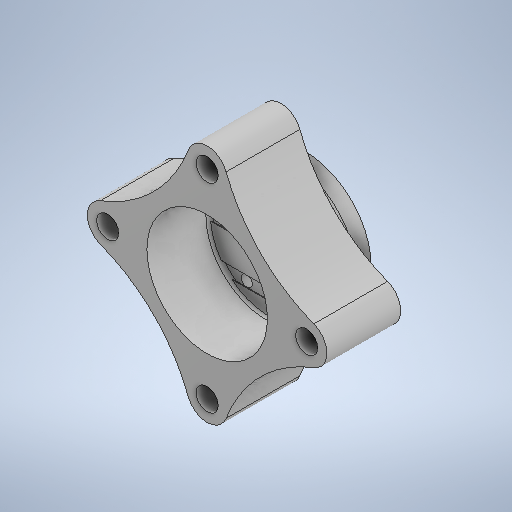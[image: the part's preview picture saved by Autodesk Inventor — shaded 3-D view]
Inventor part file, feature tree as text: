
AUTODESK INVENTOR PART (.ipt)
format: ipt  version: 2025.2 (Build 292293000, 293)  size: 745,984 bytes
history: native  units: in
note: dims shown in document units (in); Inventor stores cm internally (conversion verified against a paired STEP export)
features: sketch x16, extrude x13, projected_geometry x4, fillet x2, plane x1
ambient origin geometry x8: Origin, YZ Plane, XZ Plane, XY Plane, X Axis, Y Axis, Z Axis, Center Point
bodies: Solid1 (feature_tree), Body3 (feature_tree)
feature tree (36):
  extrude  "Extrusion1"  Depth=0.3937in TaperAngle=0.0deg
  extrude  "Extrusion2"  [1 undecoded]
  extrude  "Extrusion3"  Depth=0.315in TaperAngle=0.0deg
  plane  "Work Plane1"
  extrude  "Extrusion4"  Depth=0.2362in
  sketch  "Sketch5"  dims[d21=0.4724in d22=0.0in d23=0.0591in d24=0.0in]
  extrude  "Extrusion5"  TaperAngle=0.0deg  [1 undecoded]
  extrude  "Extrusion6"  Depth=0.3937in TaperAngle=0.0deg
  extrude  "Extrusion7"  Depth=0.0591in TaperAngle=0.0deg
  extrude  "Extrusion8"  Depth=0.1654in
  extrude  "Extrusion9"  TaperAngle=0.0deg  [1 undecoded]
  extrude  "Extrusion10"  Depth=0.1181in
  fillet  "Fillet1"  Radius=0.1181in
  extrude  "Extrusion11"  Depth=0.1181in
  extrude  "Extrusion12"  TaperAngle=0.0deg  [1 undecoded]
  fillet  "Fillet2"  Radius=0.0984in
  extrude  "Extrusion13"  TaperAngle=0.0deg  [1 undecoded]
  sketch  "Sketch1"  dims[d0=0.3937in d1=0.0in d2=0.3937in d3=0.0in]
  sketch  "Sketch2"  dims[d7=2.5591in d8=0.315in d9=0.0in]
  projected_geometry  "Projected Loop1"
  sketch  "Sketch3"  dims[d12=1.5748in d14=360.0deg d16=0.0in d17=0.0in]
  sketch  "Sketch4"  dims[d18=0.1181in d19=0.3937in d20=0.0in]
  sketch  "Sketch6"  dims[d25=0.1654in d26=0.1654in]
  sketch  "Sketch Circular Pattern1"  dims[d4=0.3937in d5=0.0in d6=-0.1181in]
  sketch  "Sketch7"  dims[d27=0.1654in d28=0.0in d29=0.0in]
  sketch  "Sketch8"  dims[d30=0.1181in d31=0.1181in d32=0.1181in]
  projected_geometry  "Projected Loop2"
  sketch  "Sketch9"  dims[d33=0.1181in d34=0.1181in]
  projected_geometry  "Projected Loop3"
  sketch  "Sketch10"  dims[d35=0.1181in d36=0.0in d37=0.0in d38=0.0984in]
  sketch  "Sketch11"  dims[d39=1.5748in d41=360.0deg d43=0.0in d44=0.0in]
  sketch  "Sketch12"  dims[d45=0.3031in]
  projected_geometry  "Projected Loop4"
  sketch  "Sketch Circular Pattern2"  dims[d10=2.126in d11=0.2362in]
  sketch  "Sketch13"  dims[d46=0.0in d47=0.0in]
  sketch  "Sketch14"  dims[d48=0.0394in d49=0.0079in d50=0.0in d40=0.0in]
note: 5 required parameter values undecoded (feature->parameter linkage not recoverable at this tier; creation-order binding heuristic only, values carry confidence <= 0.55)
